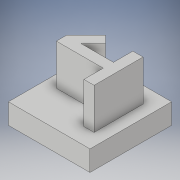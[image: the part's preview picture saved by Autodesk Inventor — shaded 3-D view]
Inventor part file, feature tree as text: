
AUTODESK INVENTOR PART (.ipt)
format: ipt  version: 2019 (Build 230136000, 136)  size: 119,808 bytes
history: native  units: mm
features: extrude x2, sketch x2
ambient origin geometry x8: Origin, YZ Plane, XZ Plane, XY Plane, X Axis, Y Axis, Z Axis, Center Point
bodies: Solid1 (feature_tree)
feature tree (4):
  extrude  "Extrusion1"  Depth=20.0mm
  extrude  "Extrusion2"  Depth=2.5mm
  sketch  "Sketch1"  dims[d0=20.0mm d1=20.0mm]
  sketch  "Sketch2"  dims[d2=5.0mm d3=0.0mm d13=2.5mm d14=2.5mm d15=2.5mm d16=2.5mm d17=3.0mm d18=12.0mm d19=3.0mm d20=3.0mm d21=45.0deg d22=10.0mm d23=0.0mm]
